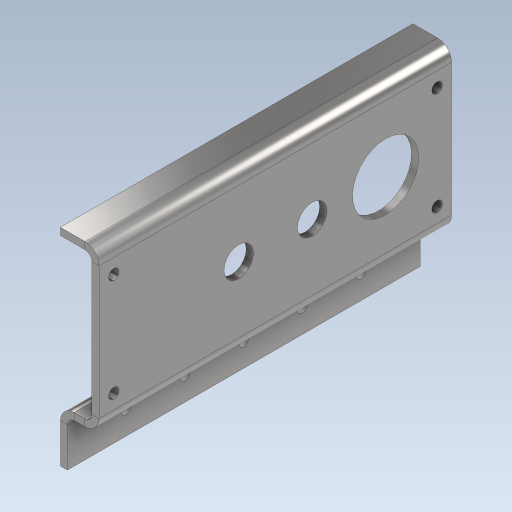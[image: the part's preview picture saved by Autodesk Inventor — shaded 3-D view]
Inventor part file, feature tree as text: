
AUTODESK INVENTOR PART (.ipt)
format: ipt  version: 2023 (Build 270158000, 158)  size: 272,896 bytes
history: native  units: in
note: dims shown in document units (in); Inventor stores cm internally (conversion verified against a paired STEP export)
features: sheet_metal_op x15, sketch x7, other x6, hole x2, projected_geometry x2
ambient origin geometry x8: Origin, YZ Plane, XZ Plane, XY Plane, X Axis, Y Axis, Z Axis, Center Point
bodies: Body1 (feature_tree)
feature tree (32):
  sheet_metal_op  "Face2"
  sheet_metal_op  "Flange1"
  sheet_metal_op  "Flange4"
  hole  "Hole2"  [1 undecoded]
  hole  "Hole1"  [1 undecoded]
  sheet_metal_op  "Face3"
  sheet_metal_op  "Flange2"
  sheet_metal_op  "Flange3"
  other  "Plate2"
  sketch  "Sketch2"  dims[d0=2.25in d1=6.0in]
  other  "Plate3"
  sheet_metal_op  "Bend1"
  sheet_metal_op  "Corner1"
  sketch  "Sketch3"  dims[d3=1.25in d4=1.25in]
  projected_geometry  "Projected Loop1"
  sketch  "Sketch4"  dims[d7=0.5in]
  other  "Plate4"
  sheet_metal_op  "Bend2"
  sketch  "Sketch5"  dims[d8=1.125in]
  other  "Plate5"
  sheet_metal_op  "Bend3"
  sheet_metal_op  "Corner2"
  sketch  "Sketch6"  dims[d10=0.12in]
  other  "Plate6"
  sheet_metal_op  "Bend4"
  sheet_metal_op  "Corner3"
  sketch  "Sketch7"  dims[d11=0.177in]
  other  "Plate7"
  sheet_metal_op  "Bend5"
  sheet_metal_op  "Corner4"
  sketch  "Sketch8"  dims[d12=5.5in d13=1.75in d14=0.5in d15=6.0in d16=0.5in d17=6.0in d18=0.12in d19=0.06in d20=0.24in d21=0.12in d22=0.6583in d23=90.0deg d24=0.12in d25=0.48in d26=0.12in d27=0.12in d28=1.0in d29=1.9685in d31=1.0in d32=0.3937in d34=1.0in d36=0.1628in d37=5.0in d38=0.22in d39=0.44in d40=0.5635in d41=0.12in d42=0.8108in d44=3.75in d45=15.748in d46=0.12in d47=0.12in d48=0.06in d49=0.24in d50=0.12in d51=0.12in d52=0.06in d53=0.24in d54=0.12in d55=0.75in d56=90.0deg d57=0.12in d58=0.48in d59=0.12in d60=0.12in d61=0.12in d62=0.06in d63=0.24in d64=0.12in d65=0.75in d66=90.0deg d67=0.12in d68=0.48in d69=0.12in d70=0.12in d71=0.75in d72=0.75in d73=0.75in d74=1.125in d75=0.5in d76=1.125in d77=1.5748in d79=2.25in d80=0.3937in d82=1.0in d84=0.12in d85=0.06in d86=0.24in d87=0.12in d88=0.7874in d89=90.0deg d90=0.12in d91=0.48in d92=0.12in d93=0.12in d94=0.3937in d95=1.0in d96=1.9685in d98=1.0in d99=0.3937in d101=1.0in d103=0.1628in d104=5.0in d105=0.375in d106=0.25in d107=0.5635in d108=1.0in d109=0.8108in]
  projected_geometry  "Projected Loop2"
note: 2 required parameter values undecoded (feature->parameter linkage not recoverable at this tier; creation-order binding heuristic only, values carry confidence <= 0.55)
